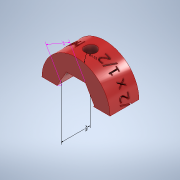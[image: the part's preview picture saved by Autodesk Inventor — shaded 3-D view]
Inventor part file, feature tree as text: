
AUTODESK INVENTOR PART (.ipt)
format: ipt  version: 2022.1 (Build 261234000, 234)  size: 824,320 bytes
history: native  units: in
note: dims shown in document units (in); Inventor stores cm internally (conversion verified against a paired STEP export)
features: other x4, sketch x4, extrude x2, thicken_offset x1, plane x1, emboss x1, hole x1, split x1
ambient origin geometry x8: Origin, YZ Plane, XZ Plane, XY Plane, X Axis, Y Axis, Z Axis, Center Point
bodies: Solid1 (feature_tree)
feature tree (15):
  other  "Annotations"
  extrude  "Extrusion1"  Depth=0.5in
  thicken_offset  "Thicken2"
  plane  "Work Plane1"
  emboss  "Emboss1"
  hole  "Hole1"  [1 undecoded]
  extrude  "Extrusion2"  Depth=0.0225in
  split  "Split1"
  sketch  "Sketch1"  dims[d0=0.5in d2=1.125in]
  sketch  "Sketch2"  dims[d3=0.2738in d4=0.5in d5=0.0in]
  sketch  "Sketch3"  dims[d8=0.0225in d9=0.0225in]
  sketch  "Sketch4"  dims[d17=1.0in d18=0.25in d19=0.1in d20=0.0in d21=0.17in d22=0.75in d23=0.5in d24=0.093in d25=0.5635in d26=0.25in d27=0.0in d28=0.2388in d29=0.2388in d30=0.191in d31=0.2186in d32=0.0in d10=0.5245in d11=1.125in d12=0.1538in d13=0.545in d14=0.1112in d15=0.3058in d16=0.4775in]
  other  "Diameter Dimension 1"
  other  "Linear Dimension 1"
  other  "Linear Dimension 2"
note: 1 required parameter value undecoded (feature->parameter linkage not recoverable at this tier; creation-order binding heuristic only, values carry confidence <= 0.55)
